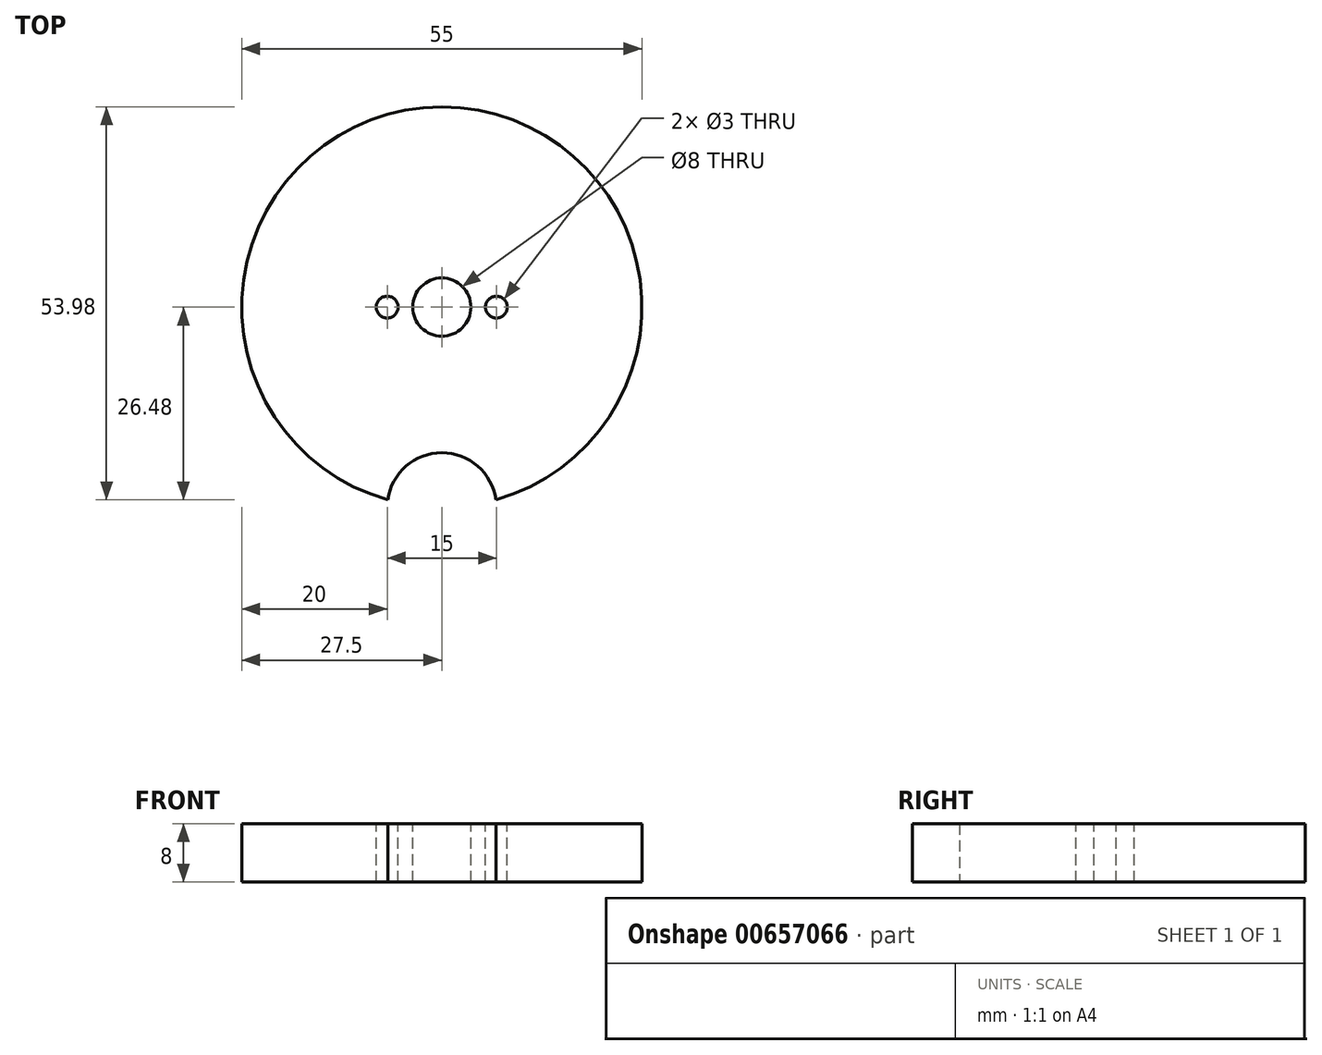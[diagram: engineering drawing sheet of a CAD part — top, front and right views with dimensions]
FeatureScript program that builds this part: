
annotation { "Feature Type Name" : "Feature", "Feature Type Description" : "" }
export const myFeature = defineFeature(function(context is Context, id is Id, definition is map)
    precondition{}
    {
        {
            var Q0;
            Q0=qCreatedBy(makeId("Front.planeOp"),FACE);
            var sketch = newSketch(context, id + "F0", { "sketchPlane" : qUnion([Q0])});
            skCircle(sketch, "E0", {"center": v(0, 0) * mm, "radius": 27.5 * mm});
            skSolve(sketch);
        }
        {
            var Q0;
            Q0 = qSketchRegion(id + "F0", true);
            extrude(context, id + "F1", {"entities" : qUnion([Q0]), "depth" : 8 * mm, "offsetDistance" : 25 * mm});
        }
        {
            var Q0;
            Q0=makeQuery(id+"F1.opExtrude","CAP_FACE",FACE,{"disambiguationData":[OSD([sQuery(id+"F0.wireOp",EDGE,"E0")])],"isStart":false});
            var sketch = newSketch(context, id + "F2", { "sketchPlane" : qUnion([Q0])});
            skCircle(sketch, "E1", {"center": v(0, 27.5) * mm, "radius": 7.5 * mm});
            skSolve(sketch);
        }
        {
            var Q0;
            Q0=qCreatedBy(makeId("Top.planeOp"),FACE);
            var sketch = newSketch(context, id + "F3", { "sketchPlane" : qUnion([Q0])});
            skLineSegment(sketch, "E2", {"start": v(0, 30.42) * mm, "end": v(0, -53.1) * mm});
            skSolve(sketch);
        }
        {
            var Q0;
            Q0 = qSketchRegion(id + "F2", true);
            extrude(context, id + "F4", {"entities" : qUnion([Q0]), "operationType" : NewBodyOperationType.REMOVE, "oppositeDirection" : true, "depth" : 25 * mm, "offsetDistance" : 25 * mm});
        }
        {
            var Q0;
            Q0=makeQuery(id+"F1.opExtrude","CAP_FACE",FACE,{"disambiguationData":[OSD([sQuery(id+"F0.wireOp",EDGE,"E0")])],"isStart":true});
            var sketch = newSketch(context, id + "F5", { "sketchPlane" : qUnion([Q0])});
            skCircle(sketch, "E3", {"center": v(0, 0) * mm, "radius": 4 * mm});
            skSolve(sketch);
        }
        {
            var Q0;
            Q0=makeQuery(id+"F5.imprint","IMPRINT",FACE,{"disambiguationData":[TD([[makeQuery(id+"F5.imprint","IMPRINT",EDGE,{"derivedFrom":sQuery(id+"F5.wireOp",EDGE,"E3")}),1.0]])]});
            extrude(context, id + "F6", {"entities" : qUnion([Q0]), "operationType" : NewBodyOperationType.REMOVE, "oppositeDirection" : true, "depth" : 50 * mm, "offsetDistance" : 25 * mm});
        }
        {
            var Q0;
            Q0=qCreatedBy(makeId("Front.planeOp"),FACE);
            var sketch = newSketch(context, id + "F7", { "sketchPlane" : qUnion([Q0])});
            skCircle(sketch, "E4", {"center": v(-7.5, 0) * mm, "radius": 1.5 * mm});
            skCircle(sketch, "E5", {"center": v(7.5, 0) * mm, "radius": 1.5 * mm});
            skSolve(sketch);
        }
        {
            var Q0;
            Q0 = qSketchRegion(id + "F7", true);
            extrude(context, id + "F8", {"entities" : qUnion([Q0]), "operationType" : NewBodyOperationType.REMOVE, "depth" : 25 * mm, "offsetDistance" : 25 * mm});
        }
        {
            var Q0;
            Q0=qCreatedBy(makeId("Front.planeOp"),FACE);
            var sketch = newSketch(context, id + "F9", { "sketchPlane" : qUnion([Q0])});
            skLineSegment(sketch, "E6", {"start": v(-64.4, 0) * mm, "end": v(65.38, 0) * mm, "construction": true});
            skLineSegment(sketch, "E7", {"start": v(0, 62.93) * mm, "end": v(0, -58.37) * mm, "construction": true});
            skSolve(sketch);
        }
        {
            var Q0;
            Q0=makeQuery(id+"F1.opExtrude","SWEPT_BODY",BODY,{"disambiguationData":[OSD([sQuery(id+"F0.wireOp",EDGE,"E0")])]});
            var Q1;
            Q1=sQuery(id+"F9.wireOp",EDGE,"E6");
            transform(context, id + "F10", {"entities" : qUnion([Q0]), "transformType" : TransformType.ROTATION, "transformAxis" : qUnion([Q1]), "angle" : 90 * degree, "makeCopy" : false});
        }
    });
